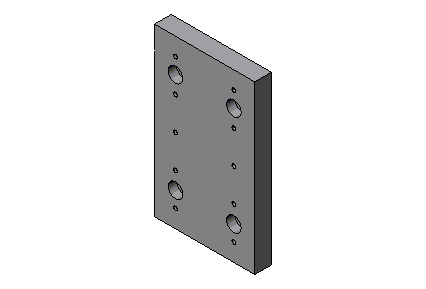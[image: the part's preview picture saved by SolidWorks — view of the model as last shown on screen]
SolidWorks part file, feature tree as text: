
SOLIDWORKS PART (.sldprt)
format: sldprt  version: not decoded by parser v0  size: 236,032 bytes
history: native  units: mm
features: thread x10, sketch x5, hole x2, extrude x1 (+10 scaffold rows collapsed)
feature tree (28):
  scaffold x10  (default folders/planes/origin — collapsed)
  sketch  "Sketch1"  dims[D1=76.2mm D2=127.0mm]
  extrude  "Extrude1"  Depth=12.7mm
  hole  "CBORE for 1/4 Socket Head Cap Screw1"  Diameter=6.5278mm Depth=12.7mm
  sketch  "Sketch3"  dims[D1=44.45mm D2=76.2mm]
  sketch  "Sketch2"  dims[hole-wizard template sketch: 41 standard entries collapsed; hole parameters kept: c12.Thru Hole Dia.=6.5278mm c12.Thru Hole Depth=12.7mm c12.C'Bore Dia.=11.1125mm c12.C'Bore Depth=6.35mm]
  hole  "M3x0.5 Tapped Hole1"  Diameter=2.5mm Depth=12.7mm
  sketch  "Sketch5"  dims[D1=25.0mm D2=25.0mm D3=25.0mm D4=25.0mm D5=25.0mm D6=25.0mm D7=25.0mm D8=25.0mm D9=44.45mm]
  sketch  "Sketch4"  dims[hole-wizard template sketch: 60 standard entries collapsed; hole parameters kept: c18.Thru Tap Drill Depth=12.7mm]
  thread  "Cosmetic Thread1"  Diameter=5.999988mm  [1 undecoded]
  thread  "Cosmetic Thread2"  Diameter=5.999988mm  [1 undecoded]
  thread  "Cosmetic Thread3"  Diameter=5.999988mm  [1 undecoded]
  thread  "Cosmetic Thread4"  Diameter=5.999988mm  [1 undecoded]
  thread  "Cosmetic Thread5"  Diameter=5.999988mm  [1 undecoded]
  thread  "Cosmetic Thread6"  Diameter=5.999988mm  [1 undecoded]
  thread  "Cosmetic Thread7"  Diameter=5.999988mm  [1 undecoded]
  thread  "Cosmetic Thread8"  Diameter=5.999988mm  [1 undecoded]
  thread  "Cosmetic Thread9"  Diameter=5.999988mm  [1 undecoded]
  thread  "Cosmetic Thread10"  Diameter=5.999988mm  [1 undecoded]
decode coverage: 18 of 18 modeling features carry decoded parameters
note: ~ marks probable driven/reference dimensions
note: 10 parameter values undecoded
note: suppression state not decoded; provenance and decode notes live in map.json
